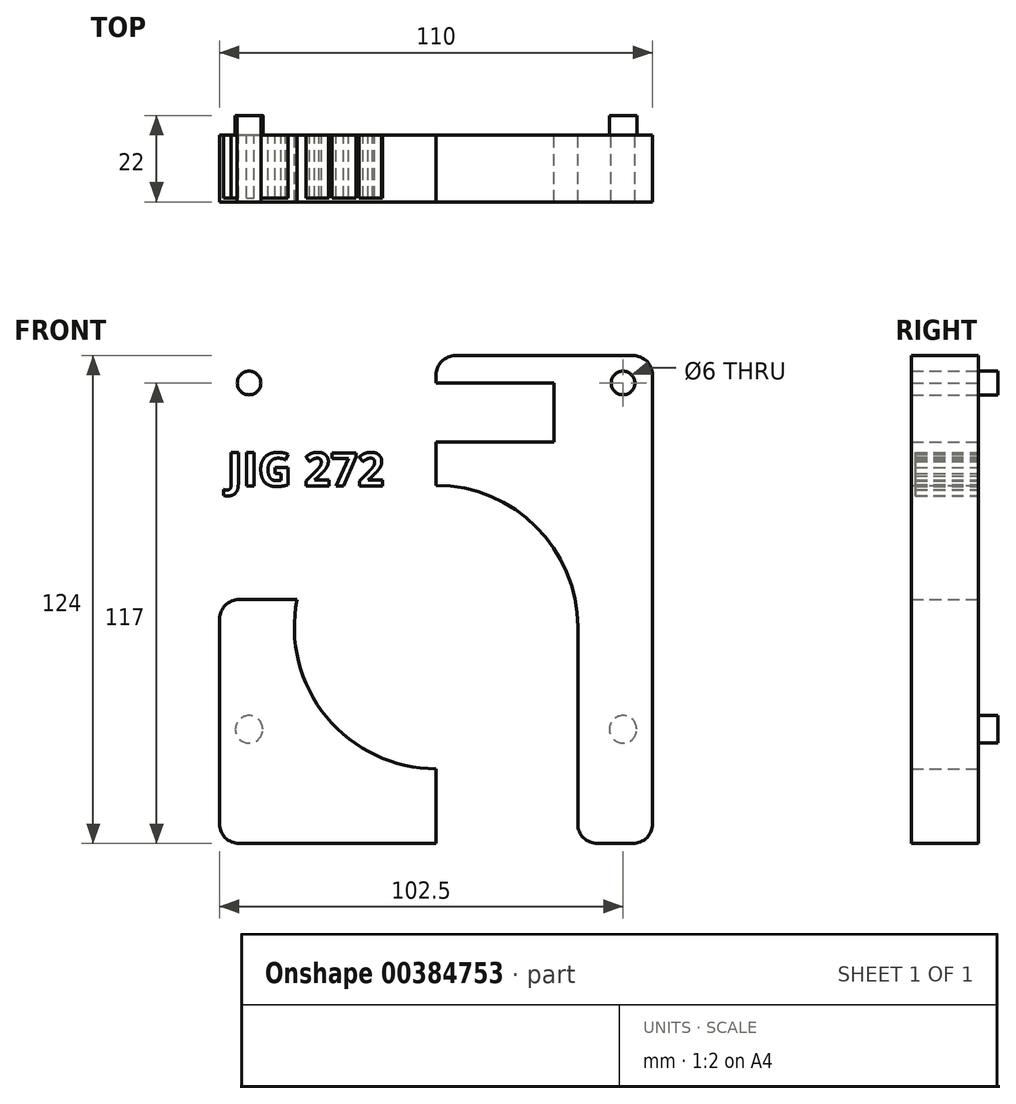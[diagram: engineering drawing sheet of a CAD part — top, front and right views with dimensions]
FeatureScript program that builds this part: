
annotation { "Feature Type Name" : "Feature", "Feature Type Description" : "" }
export const myFeature = defineFeature(function(context is Context, id is Id, definition is map)
    precondition{}
    {
        {
            var Q0;
            Q0=qCreatedBy(makeId("Front.planeOp"),FACE);
            var sketch = newSketch(context, id + "F0", { "sketchPlane" : qUnion([Q0])});
            skLineSegment(sketch, "E0", {"start": v(0, 0) * mm, "end": v(-55, 0) * mm});
            skLineSegment(sketch, "E1", {"start": v(-55, 0) * mm, "end": v(-55, 62) * mm});
            skLineSegment(sketch, "E2", {"start": v(-55, 62) * mm, "end": v(0, 62) * mm});
            skLineSegment(sketch, "E3", {"start": v(0, 62) * mm, "end": v(0, 0) * mm});
            skLineSegment(sketch, "E4.MirrorCS", {"start": v(55, 62) * mm, "end": v(0, 62) * mm});
            skLineSegment(sketch, "E5.MirrorCS", {"start": v(55, 0) * mm, "end": v(55, 62) * mm});
            skLineSegment(sketch, "E6.MirrorCS", {"start": v(-55, 0) * mm, "end": v(-55, -62) * mm});
            skLineSegment(sketch, "E7.MirrorCS", {"start": v(-55, -62) * mm, "end": v(0, -62) * mm});
            skLineSegment(sketch, "E8.MirrorCS", {"start": v(55, -62) * mm, "end": v(0, -62) * mm});
            skLineSegment(sketch, "E9.MirrorCS", {"start": v(55, 0) * mm, "end": v(55, -62) * mm});
            skLineSegment(sketch, "E10", {"start": v(-55, -62) * mm, "end": v(-47.5, -62) * mm});
            skLineSegment(sketch, "E11", {"start": v(-47.5, -62) * mm, "end": v(-47.5, -33) * mm});
            skLineSegment(sketch, "E12.MirrorCS", {"start": v(47.5, -62) * mm, "end": v(47.5, -33) * mm});
            skCircle(sketch, "E13", {"center": v(-47.5, -33) * mm, "radius": 3.5 * mm});
            skCircle(sketch, "E14", {"center": v(47.5, -33) * mm, "radius": 3.5 * mm});
            skLineSegment(sketch, "E15", {"start": v(-47.5, -33) * mm, "end": v(-47.5, 55) * mm});
            skCircle(sketch, "E16", {"center": v(-47.5, 55) * mm, "radius": 3 * mm});
            skCircle(sketch, "E17.MirrorC", {"center": v(47.5, 55) * mm, "radius": 3 * mm});
            skLineSegment(sketch, "E18", {"start": v(0, -62) * mm, "end": v(-36, -62) * mm});
            skLineSegment(sketch, "E19.MirrorCS", {"start": v(0, -62) * mm, "end": v(36, -62) * mm});
            skLineSegment(sketch, "E20", {"start": v(-36, 0) * mm, "end": v(-36, -62) * mm});
            skLineSegment(sketch, "E21", {"start": v(36, -62) * mm, "end": v(36, 0) * mm});
            skLineSegment(sketch, "E22", {"start": v(47.5, 55) * mm, "end": v(47.5, -33) * mm});
            skLineSegment(sketch, "E23", {"start": v(0, -62) * mm, "end": v(0, -7) * mm});
            skCircle(sketch, "E24", {"center": v(0, -7) * mm, "radius": 36 * mm});
            skLineSegment(sketch, "E25", {"start": v(0, 55) * mm, "end": v(-30, 55) * mm});
            skLineSegment(sketch, "E26", {"start": v(-30, 55) * mm, "end": v(-30, 40) * mm});
            skLineSegment(sketch, "E27", {"start": v(-30, 40) * mm, "end": v(0, 40) * mm});
            skLineSegment(sketch, "E28.MirrorCS", {"start": v(0, 55) * mm, "end": v(30, 55) * mm});
            skLineSegment(sketch, "E29.MirrorCS", {"start": v(30, 55) * mm, "end": v(30, 40) * mm});
            skLineSegment(sketch, "E30.MirrorCS", {"start": v(30, 40) * mm, "end": v(0, 40) * mm});
            skText(sketch, "E31", { "text": "JIG 272", "fontName": "OpenSans-Bold.ttf"});
            const initialGuessF0  = {"E31": [-0.0531, 0.0288, 1, 0, 0.00856]};
            skSetInitialGuess(sketch, initialGuessF0);
            skSolve(sketch);
        }
        {
            var Q0;
            {var subQ4=sQuery(id+"F0.wireOp",EDGE,"E6.MirrorCS");Q0=makeQuery(id+"F0.imprint","IMPRINT",FACE,{"disambiguationData":[TD([[makeQuery(id+"F0.imprint","IMPRINT",EDGE,{"derivedFrom":subQ4}),1.0]])]});}
            var Q1;
            {var subQ6=sQuery(id+"F0.wireOp",EDGE,"E7.MirrorCS");Q1=makeQuery(id+"F0.imprint","IMPRINT",FACE,{"disambiguationData":[TD([[makeQuery(id+"F0.imprint","IMPRINT",EDGE,{"derivedFrom":subQ6}),1.0]])]});}
            var Q2;
            {var subQ1=sQuery(id+"F0.wireOp",EDGE,"E1");Q2=makeQuery(id+"F0.imprint","IMPRINT",FACE,{"disambiguationData":[TD([[makeQuery(id+"F0.imprint","IMPRINT",EDGE,{"derivedFrom":subQ1}),-1.0]])]});}
            var Q3;
            {var subQ4=sQuery(id+"F0.wireOp",EDGE,"E4.MirrorCS");Q3=makeQuery(id+"F0.imprint","IMPRINT",FACE,{"disambiguationData":[TD([[makeQuery(id+"F0.imprint","IMPRINT",EDGE,{"derivedFrom":subQ4}),1.0]])]});}
            var Q4;
            Q4=makeQuery(id+"F0.imprint","IMPRINT",FACE,{"disambiguationData":[TD([[makeQuery(id+"F0.imprint","IMPRINT",EDGE,{"derivedFrom":sQuery(id+"F0.wireOp",EDGE,"E16")}),1.0]])]});
            var Q5;
            {var subQ0=sQuery(id+"F0.wireOp",EDGE,"E15");var subQ1=sQuery(id+"F0.wireOp",EDGE,"E11");var subQ2=makeQuery(id+"F0.imprint","INTERSECT",VERTEX,{"derivedFrom":[subQ1,subQ0]});Q5=makeQuery(id+"F0.imprint","IMPRINT",FACE,{"disambiguationData":[TD([[makeQuery(id+"F0.imprint","IMPRINT",EDGE,{"disambiguationData":[TD([[subQ2,1.0]])],"derivedFrom":subQ1}),-1.0]])]});}
            var Q6;
            {var subQ0=sQuery(id+"F0.wireOp",EDGE,"E15");var subQ1=sQuery(id+"F0.wireOp",EDGE,"E11");var subQ2=makeQuery(id+"F0.imprint","INTERSECT",VERTEX,{"derivedFrom":[subQ1,subQ0]});Q6=makeQuery(id+"F0.imprint","IMPRINT",FACE,{"disambiguationData":[TD([[makeQuery(id+"F0.imprint","IMPRINT",EDGE,{"disambiguationData":[TD([[subQ2,1.0]])],"derivedFrom":subQ1}),1.0]])]});}
            var Q7;
            Q7=makeQuery(id+"F0.imprint","IMPRINT",FACE,{"disambiguationData":[TD([[makeQuery(id+"F0.imprint","IMPRINT",EDGE,{"derivedFrom":sQuery(id+"F0.wireOp",EDGE,"E14")}),1.0]])]});
            var Q8;
            Q8=makeQuery(id+"F0.imprint","IMPRINT",FACE,{"disambiguationData":[TD([[makeQuery(id+"F0.imprint","IMPRINT",EDGE,{"derivedFrom":sQuery(id+"F0.wireOp",EDGE,"E17.MirrorC")}),-1.0]])]});
            var Q9;
            {var subQ0=sQuery(id+"F0.wireOp",EDGE,"E20");var subQ3=sQuery(id+"F0.wireOp",EDGE,"MsqNyLX8-3hiH-o9ip-gQ6e-HD20fMBUYYWa");var subQ5=makeQuery(id+"F0.imprint","INTERSECT",VERTEX,{"derivedFrom":[subQ0,subQ3]});Q9=makeQuery(id+"F0.imprint","IMPRINT",FACE,{"disambiguationData":[TD([[makeQuery(id+"F0.imprint","IMPRINT",EDGE,{"disambiguationData":[TD([[subQ5,1.0]])],"derivedFrom":subQ0}),-1.0]])]});}
            var Q10;
            {var subQ1=sQuery(id+"F0.wireOp",EDGE,"E8.MirrorCS");var subQ5=sQuery(id+"F0.wireOp",EDGE,"E12.MirrorCS");var subQ6=makeQuery(id+"F0.imprint","INTERSECT",VERTEX,{"derivedFrom":[subQ1,subQ5]});Q10=makeQuery(id+"F0.imprint","IMPRINT",FACE,{"disambiguationData":[TD([[makeQuery(id+"F0.imprint","IMPRINT",EDGE,{"disambiguationData":[TD([[subQ6,-1.0]])],"derivedFrom":subQ5}),1.0]])]});}
            var Q11;
            {var subQ0=sQuery(id+"F0.wireOp",EDGE,"E20");var subQ1=sQuery(id+"F0.wireOp",EDGE,"E0");var subQ2=makeQuery(id+"F0.imprint","INTERSECT",VERTEX,{"derivedFrom":[subQ1,subQ0]});Q11=makeQuery(id+"F0.imprint","IMPRINT",FACE,{"disambiguationData":[TD([[makeQuery(id+"F0.imprint","IMPRINT",EDGE,{"disambiguationData":[TD([[subQ2,1.0]])],"derivedFrom":subQ1}),1.0]])]});}
            var Q12;
            Q12=makeQuery(id+"F0.imprint","IMPRINT",FACE,{"disambiguationData":[TD([[makeQuery(id+"F0.imprint","IMPRINT",EDGE,{"derivedFrom":sQuery(id+"F0.wireOp",EDGE,"E31.sketch_text.stroke-0")}),-1.0]])]});
            var Q13;
            {var subQ5=sQuery(id+"F0.wireOp",EDGE,"E31.sketch_text.stroke-12");Q13=makeQuery(id+"F0.imprint","IMPRINT",FACE,{"disambiguationData":[TD([[makeQuery(id+"F0.imprint","IMPRINT",EDGE,{"derivedFrom":subQ5}),-1.0]])]});}
            var Q14;
            Q14=makeQuery(id+"F0.imprint","IMPRINT",FACE,{"disambiguationData":[TD([[makeQuery(id+"F0.imprint","IMPRINT",EDGE,{"derivedFrom":sQuery(id+"F0.wireOp",EDGE,"E31.sketch_text.stroke-14")}),-1.0]])]});
            var Q15;
            Q15=makeQuery(id+"F0.imprint","IMPRINT",FACE,{"disambiguationData":[TD([[makeQuery(id+"F0.imprint","IMPRINT",EDGE,{"derivedFrom":sQuery(id+"F0.wireOp",EDGE,"E31.sketch_text.stroke-33")}),-1.0]])]});
            var Q16;
            Q16=makeQuery(id+"F0.imprint","IMPRINT",FACE,{"disambiguationData":[TD([[makeQuery(id+"F0.imprint","IMPRINT",EDGE,{"derivedFrom":sQuery(id+"F0.wireOp",EDGE,"E31.sketch_text.stroke-57")}),-1.0]])]});
            var Q17;
            Q17=makeQuery(id+"F0.imprint","IMPRINT",FACE,{"disambiguationData":[TD([[makeQuery(id+"F0.imprint","IMPRINT",EDGE,{"derivedFrom":sQuery(id+"F0.wireOp",EDGE,"E31.sketch_text.stroke-64")}),-1.0]])]});
            var Q18;
            {var subQ5=sQuery(id+"F0.wireOp",EDGE,"E31.sketch_text.stroke-10");Q18=makeQuery(id+"F0.imprint","IMPRINT",FACE,{"disambiguationData":[TD([[makeQuery(id+"F0.imprint","IMPRINT",EDGE,{"derivedFrom":subQ5}),-1.0]])]});}
            extrude(context, id + "F1", {"entities" : qUnion([Q0, Q1, Q2, Q3, Q4, Q5, Q6, Q7, Q8, Q9, Q10, Q11, Q12, Q13, Q14, Q15, Q16, Q17, Q18]), "depth" : 17 * mm});
        }
        {
            var Q0;
            Q0=makeQuery(id+"F0.imprint","IMPRINT",FACE,{"disambiguationData":[TD([[makeQuery(id+"F0.imprint","IMPRINT",EDGE,{"derivedFrom":sQuery(id+"F0.wireOp",EDGE,"E16")}),1.0]])]});
            var Q1;
            {var subQ0=sQuery(id+"F0.wireOp",EDGE,"E15");var subQ1=sQuery(id+"F0.wireOp",EDGE,"E11");var subQ2=makeQuery(id+"F0.imprint","INTERSECT",VERTEX,{"derivedFrom":[subQ1,subQ0]});Q1=makeQuery(id+"F0.imprint","IMPRINT",FACE,{"disambiguationData":[TD([[makeQuery(id+"F0.imprint","IMPRINT",EDGE,{"disambiguationData":[TD([[subQ2,1.0]])],"derivedFrom":subQ1}),1.0]])]});}
            var Q2;
            {var subQ0=sQuery(id+"F0.wireOp",EDGE,"E15");var subQ1=sQuery(id+"F0.wireOp",EDGE,"E11");var subQ2=makeQuery(id+"F0.imprint","INTERSECT",VERTEX,{"derivedFrom":[subQ1,subQ0]});Q2=makeQuery(id+"F0.imprint","IMPRINT",FACE,{"disambiguationData":[TD([[makeQuery(id+"F0.imprint","IMPRINT",EDGE,{"disambiguationData":[TD([[subQ2,1.0]])],"derivedFrom":subQ1}),-1.0]])]});}
            var Q3;
            Q3=makeQuery(id+"F0.imprint","IMPRINT",FACE,{"disambiguationData":[TD([[makeQuery(id+"F0.imprint","IMPRINT",EDGE,{"derivedFrom":sQuery(id+"F0.wireOp",EDGE,"E17.MirrorC")}),-1.0]])]});
            var Q4;
            Q4=makeQuery(id+"F0.imprint","IMPRINT",FACE,{"disambiguationData":[TD([[makeQuery(id+"F0.imprint","IMPRINT",EDGE,{"derivedFrom":sQuery(id+"F0.wireOp",EDGE,"E14")}),1.0]])]});
            extrude(context, id + "F2", {"entities" : qUnion([Q0, Q1, Q2, Q3, Q4]), "operationType" : NewBodyOperationType.ADD, "oppositeDirection" : true, "depth" : 5 * mm});
        }
        {
            var Q0;
            Q0=makeQuery(id+"F1.opExtrude","SWEPT_EDGE",EDGE,{"disambiguationData":[OSD([sQuery(id+"F0.wireOp",EDGE,"E1"),sQuery(id+"F0.wireOp",EDGE,"E2")])]});
            var Q1;
            Q1=makeQuery(id+"F1.opExtrude","SWEPT_EDGE",EDGE,{"disambiguationData":[OSD([sQuery(id+"F0.wireOp",EDGE,"E4.MirrorCS"),sQuery(id+"F0.wireOp",EDGE,"E5.MirrorCS")])]});
            var Q2;
            Q2=makeQuery(id+"F1.opExtrude","SWEPT_EDGE",EDGE,{"disambiguationData":[OSD([sQuery(id+"F0.wireOp",EDGE,"E6.MirrorCS"),sQuery(id+"F0.wireOp",EDGE,"E10")])]});
            var Q3;
            Q3=makeQuery(id+"F1.opExtrude","SWEPT_EDGE",EDGE,{"disambiguationData":[OSD([sQuery(id+"F0.wireOp",EDGE,"E7.MirrorCS"),sQuery(id+"F0.wireOp",EDGE,"E18"),sQuery(id+"F0.wireOp",EDGE,"E20")])]});
            var Q4;
            Q4=makeQuery(id+"F1.opExtrude","SWEPT_EDGE",EDGE,{"disambiguationData":[OSD([sQuery(id+"F0.wireOp",EDGE,"E8.MirrorCS"),sQuery(id+"F0.wireOp",EDGE,"E19.MirrorCS"),sQuery(id+"F0.wireOp",EDGE,"E21")])]});
            var Q5;
            Q5=makeQuery(id+"F1.opExtrude","SWEPT_EDGE",EDGE,{"disambiguationData":[OSD([sQuery(id+"F0.wireOp",EDGE,"E8.MirrorCS"),sQuery(id+"F0.wireOp",EDGE,"E9.MirrorCS")])]});
            fillet(context, id + "F3", {"entities" : qUnion([Q0, Q1, Q2, Q3, Q4, Q5]), "radius" : 5 * mm, "tangentPropagation" : true, "allowEdgeOverflow" : false});
        }
        {
            var Q0;
            Q0=makeQuery(id+"F0.imprint","IMPRINT",FACE,{"disambiguationData":[TD([[makeQuery(id+"F0.imprint","IMPRINT",EDGE,{"derivedFrom":sQuery(id+"F0.wireOp",EDGE,"E31.sketch_text.stroke-0")}),-1.0]])]});
            var Q1;
            {var subQ5=sQuery(id+"F0.wireOp",EDGE,"E31.sketch_text.stroke-10");Q1=makeQuery(id+"F0.imprint","IMPRINT",FACE,{"disambiguationData":[TD([[makeQuery(id+"F0.imprint","IMPRINT",EDGE,{"derivedFrom":subQ5}),-1.0]])]});}
            var Q2;
            {var subQ5=sQuery(id+"F0.wireOp",EDGE,"E31.sketch_text.stroke-12");Q2=makeQuery(id+"F0.imprint","IMPRINT",FACE,{"disambiguationData":[TD([[makeQuery(id+"F0.imprint","IMPRINT",EDGE,{"derivedFrom":subQ5}),-1.0]])]});}
            var Q3;
            Q3=makeQuery(id+"F0.imprint","IMPRINT",FACE,{"disambiguationData":[TD([[makeQuery(id+"F0.imprint","IMPRINT",EDGE,{"derivedFrom":sQuery(id+"F0.wireOp",EDGE,"E31.sketch_text.stroke-14")}),-1.0]])]});
            var Q4;
            Q4=makeQuery(id+"F0.imprint","IMPRINT",FACE,{"disambiguationData":[TD([[makeQuery(id+"F0.imprint","IMPRINT",EDGE,{"derivedFrom":sQuery(id+"F0.wireOp",EDGE,"E31.sketch_text.stroke-33")}),-1.0]])]});
            var Q5;
            Q5=makeQuery(id+"F0.imprint","IMPRINT",FACE,{"disambiguationData":[TD([[makeQuery(id+"F0.imprint","IMPRINT",EDGE,{"derivedFrom":sQuery(id+"F0.wireOp",EDGE,"E31.sketch_text.stroke-57")}),-1.0]])]});
            var Q6;
            Q6=makeQuery(id+"F0.imprint","IMPRINT",FACE,{"disambiguationData":[TD([[makeQuery(id+"F0.imprint","IMPRINT",EDGE,{"derivedFrom":sQuery(id+"F0.wireOp",EDGE,"E31.sketch_text.stroke-64")}),-1.0]])]});
            extrude(context, id + "F4", {"entities" : qUnion([Q0, Q1, Q2, Q3, Q4, Q5, Q6]), "operationType" : NewBodyOperationType.ADD, "depth" : 19 * mm});
        }
        {
            var Q0;
            Q0=makeQuery(id+"F4.opExtrude","CAP_FACE",FACE,{"disambiguationData":[OSD([sQuery(id+"F0.wireOp",EDGE,"E31.sketch_text.stroke-0"),sQuery(id+"F0.wireOp",EDGE,"E31.sketch_text.stroke-1"),sQuery(id+"F0.wireOp",EDGE,"E31.sketch_text.stroke-2"),sQuery(id+"F0.wireOp",EDGE,"E31.sketch_text.stroke-3"),sQuery(id+"F0.wireOp",EDGE,"E31.sketch_text.stroke-4"),sQuery(id+"F0.wireOp",EDGE,"E31.sketch_text.stroke-5"),sQuery(id+"F0.wireOp",EDGE,"E31.sketch_text.stroke-6"),sQuery(id+"F0.wireOp",EDGE,"E31.sketch_text.stroke-7"),sQuery(id+"F0.wireOp",EDGE,"E31.sketch_text.stroke-8"),sQuery(id+"F0.wireOp",EDGE,"E31.sketch_text.stroke-9")])],"isStart":false});
            var Q1;
            Q1=makeQuery(id+"F4.opExtrude","CAP_FACE",FACE,{"disambiguationData":[OSD([sQuery(id+"F0.wireOp",EDGE,"E31.sketch_text.stroke-10"),sQuery(id+"F0.wireOp",EDGE,"E31.sketch_text.stroke-11"),sQuery(id+"F0.wireOp",EDGE,"E31.sketch_text.stroke-12"),sQuery(id+"F0.wireOp",EDGE,"E31.sketch_text.stroke-13")])],"isStart":false});
            var Q2;
            Q2=makeQuery(id+"F4.opExtrude","CAP_FACE",FACE,{"disambiguationData":[OSD([sQuery(id+"F0.wireOp",EDGE,"E31.sketch_text.stroke-14"),sQuery(id+"F0.wireOp",EDGE,"E31.sketch_text.stroke-15"),sQuery(id+"F0.wireOp",EDGE,"E31.sketch_text.stroke-16"),sQuery(id+"F0.wireOp",EDGE,"E31.sketch_text.stroke-17"),sQuery(id+"F0.wireOp",EDGE,"E31.sketch_text.stroke-18"),sQuery(id+"F0.wireOp",EDGE,"E31.sketch_text.stroke-19"),sQuery(id+"F0.wireOp",EDGE,"E31.sketch_text.stroke-20"),sQuery(id+"F0.wireOp",EDGE,"E31.sketch_text.stroke-21"),sQuery(id+"F0.wireOp",EDGE,"E31.sketch_text.stroke-22"),sQuery(id+"F0.wireOp",EDGE,"E31.sketch_text.stroke-23"),sQuery(id+"F0.wireOp",EDGE,"E31.sketch_text.stroke-24"),sQuery(id+"F0.wireOp",EDGE,"E31.sketch_text.stroke-25"),sQuery(id+"F0.wireOp",EDGE,"E31.sketch_text.stroke-26"),sQuery(id+"F0.wireOp",EDGE,"E31.sketch_text.stroke-27"),sQuery(id+"F0.wireOp",EDGE,"E31.sketch_text.stroke-28"),sQuery(id+"F0.wireOp",EDGE,"E31.sketch_text.stroke-29"),sQuery(id+"F0.wireOp",EDGE,"E31.sketch_text.stroke-30"),sQuery(id+"F0.wireOp",EDGE,"E31.sketch_text.stroke-31"),sQuery(id+"F0.wireOp",EDGE,"E31.sketch_text.stroke-32")])],"isStart":false});
            var Q3;
            Q3=makeQuery(id+"F4.opExtrude","CAP_FACE",FACE,{"disambiguationData":[OSD([sQuery(id+"F0.wireOp",EDGE,"E31.sketch_text.stroke-33"),sQuery(id+"F0.wireOp",EDGE,"E31.sketch_text.stroke-34"),sQuery(id+"F0.wireOp",EDGE,"E31.sketch_text.stroke-35"),sQuery(id+"F0.wireOp",EDGE,"E31.sketch_text.stroke-36"),sQuery(id+"F0.wireOp",EDGE,"E31.sketch_text.stroke-37"),sQuery(id+"F0.wireOp",EDGE,"E31.sketch_text.stroke-38"),sQuery(id+"F0.wireOp",EDGE,"E31.sketch_text.stroke-39"),sQuery(id+"F0.wireOp",EDGE,"E31.sketch_text.stroke-40"),sQuery(id+"F0.wireOp",EDGE,"E31.sketch_text.stroke-41"),sQuery(id+"F0.wireOp",EDGE,"E31.sketch_text.stroke-42"),sQuery(id+"F0.wireOp",EDGE,"E31.sketch_text.stroke-43"),sQuery(id+"F0.wireOp",EDGE,"E31.sketch_text.stroke-44"),sQuery(id+"F0.wireOp",EDGE,"E31.sketch_text.stroke-45"),sQuery(id+"F0.wireOp",EDGE,"E31.sketch_text.stroke-46"),sQuery(id+"F0.wireOp",EDGE,"E31.sketch_text.stroke-47"),sQuery(id+"F0.wireOp",EDGE,"E31.sketch_text.stroke-48"),sQuery(id+"F0.wireOp",EDGE,"E31.sketch_text.stroke-49"),sQuery(id+"F0.wireOp",EDGE,"E31.sketch_text.stroke-50"),sQuery(id+"F0.wireOp",EDGE,"E31.sketch_text.stroke-51"),sQuery(id+"F0.wireOp",EDGE,"E31.sketch_text.stroke-52"),sQuery(id+"F0.wireOp",EDGE,"E31.sketch_text.stroke-53"),sQuery(id+"F0.wireOp",EDGE,"E31.sketch_text.stroke-54"),sQuery(id+"F0.wireOp",EDGE,"E31.sketch_text.stroke-55"),sQuery(id+"F0.wireOp",EDGE,"E31.sketch_text.stroke-56")])],"isStart":false});
            var Q4;
            Q4=makeQuery(id+"F4.opExtrude","CAP_FACE",FACE,{"disambiguationData":[OSD([sQuery(id+"F0.wireOp",EDGE,"E31.sketch_text.stroke-57"),sQuery(id+"F0.wireOp",EDGE,"E31.sketch_text.stroke-58"),sQuery(id+"F0.wireOp",EDGE,"E31.sketch_text.stroke-59"),sQuery(id+"F0.wireOp",EDGE,"E31.sketch_text.stroke-60"),sQuery(id+"F0.wireOp",EDGE,"E31.sketch_text.stroke-61"),sQuery(id+"F0.wireOp",EDGE,"E31.sketch_text.stroke-62"),sQuery(id+"F0.wireOp",EDGE,"E31.sketch_text.stroke-63")])],"isStart":false});
            var Q5;
            Q5=makeQuery(id+"F4.opExtrude","CAP_FACE",FACE,{"disambiguationData":[OSD([sQuery(id+"F0.wireOp",EDGE,"E31.sketch_text.stroke-64"),sQuery(id+"F0.wireOp",EDGE,"E31.sketch_text.stroke-65"),sQuery(id+"F0.wireOp",EDGE,"E31.sketch_text.stroke-66"),sQuery(id+"F0.wireOp",EDGE,"E31.sketch_text.stroke-67"),sQuery(id+"F0.wireOp",EDGE,"E31.sketch_text.stroke-68"),sQuery(id+"F0.wireOp",EDGE,"E31.sketch_text.stroke-69"),sQuery(id+"F0.wireOp",EDGE,"E31.sketch_text.stroke-70"),sQuery(id+"F0.wireOp",EDGE,"E31.sketch_text.stroke-71"),sQuery(id+"F0.wireOp",EDGE,"E31.sketch_text.stroke-72"),sQuery(id+"F0.wireOp",EDGE,"E31.sketch_text.stroke-73"),sQuery(id+"F0.wireOp",EDGE,"E31.sketch_text.stroke-74"),sQuery(id+"F0.wireOp",EDGE,"E31.sketch_text.stroke-75"),sQuery(id+"F0.wireOp",EDGE,"E31.sketch_text.stroke-76"),sQuery(id+"F0.wireOp",EDGE,"E31.sketch_text.stroke-77"),sQuery(id+"F0.wireOp",EDGE,"E31.sketch_text.stroke-78"),sQuery(id+"F0.wireOp",EDGE,"E31.sketch_text.stroke-79"),sQuery(id+"F0.wireOp",EDGE,"E31.sketch_text.stroke-80"),sQuery(id+"F0.wireOp",EDGE,"E31.sketch_text.stroke-81"),sQuery(id+"F0.wireOp",EDGE,"E31.sketch_text.stroke-82"),sQuery(id+"F0.wireOp",EDGE,"E31.sketch_text.stroke-83"),sQuery(id+"F0.wireOp",EDGE,"E31.sketch_text.stroke-84"),sQuery(id+"F0.wireOp",EDGE,"E31.sketch_text.stroke-85"),sQuery(id+"F0.wireOp",EDGE,"E31.sketch_text.stroke-86"),sQuery(id+"F0.wireOp",EDGE,"E31.sketch_text.stroke-87")])],"isStart":false});
            extrude(context, id + "F5", {"entities" : qUnion([Q0, Q1, Q2, Q3, Q4, Q5]), "operationType" : NewBodyOperationType.REMOVE, "oppositeDirection" : true, "depth" : 3 * mm});
        }
    });
